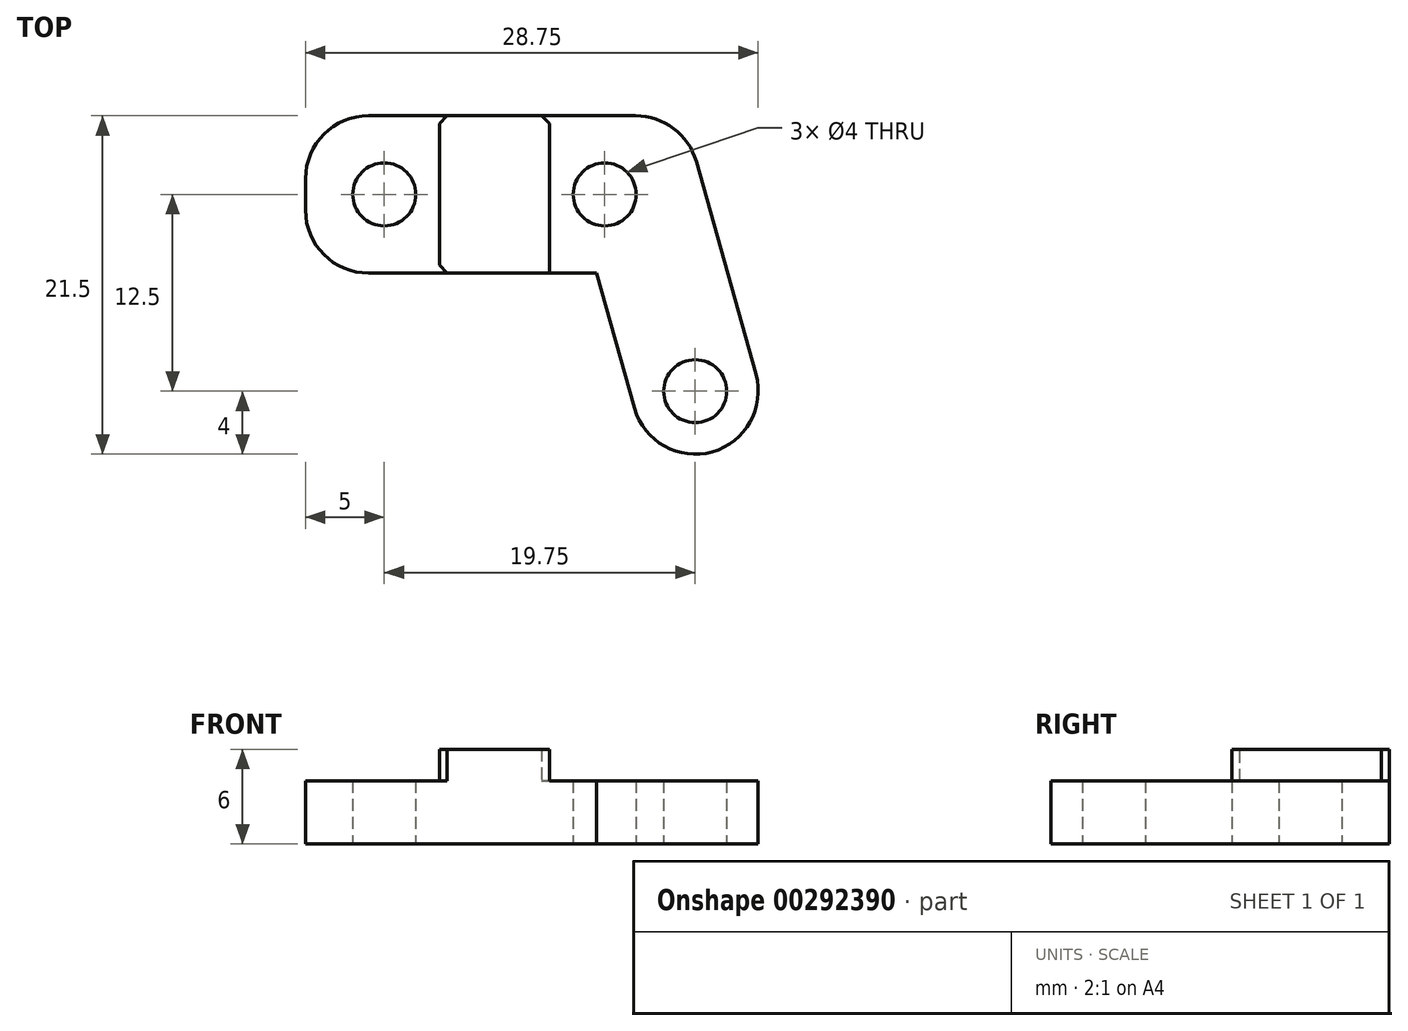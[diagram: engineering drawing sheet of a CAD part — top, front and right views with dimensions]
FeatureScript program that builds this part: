
annotation { "Feature Type Name" : "Feature", "Feature Type Description" : "" }
export const myFeature = defineFeature(function(context is Context, id is Id, definition is map)
    precondition{}
    {
        {
            var Q0;
            Q0=qCreatedBy(makeId("Top.planeOp"),FACE);
            var sketch = newSketch(context, id + "F0", { "sketchPlane" : qUnion([Q0])});
            skLineSegment(sketch, "E0.bottom", {"start": v(0, 0) * mm, "end": v(24, 0) * mm});
            skLineSegment(sketch, "E0.top", {"start": v(0, 10) * mm, "end": v(24, 10) * mm});
            skLineSegment(sketch, "E0.left", {"start": v(0, 0) * mm, "end": v(0, 10) * mm});
            skLineSegment(sketch, "E0.right", {"start": v(24, 0) * mm, "end": v(24, 10) * mm});
            skCircle(sketch, "E1", {"center": v(5, 5) * mm, "radius": 2 * mm});
            skPoint(sketch, "E1.centerSnap0", {"position": v(0, 5) * mm});
            skCircle(sketch, "E2", {"center": v(19, 5) * mm, "radius": 2 * mm});
            skSolve(sketch);
        }
        {
            var Q0;
            Q0 = qSketchRegion(id + "F0", true);
            extrude(context, id + "F1", {"entities" : qUnion([Q0]), "depth" : 4 * mm});
        }
        {
            var Q0;
            Q0=makeQuery(id+"F1.opExtrude","CAP_FACE",FACE,{"disambiguationData":[OSD([sQuery(id+"F0.wireOp",EDGE,"E0.bottom"),sQuery(id+"F0.wireOp",EDGE,"E0.top"),sQuery(id+"F0.wireOp",EDGE,"E0.left"),sQuery(id+"F0.wireOp",EDGE,"E0.right"),sQuery(id+"F0.wireOp",EDGE,"E1"),sQuery(id+"F0.wireOp",EDGE,"E2")])],"isStart":false});
            var sketch = newSketch(context, id + "F2", { "sketchPlane" : qUnion([Q0])});
            skLineSegment(sketch, "E3.bottom", {"start": v(8.5, 10) * mm, "end": v(15.5, 10) * mm});
            skLineSegment(sketch, "E3.top", {"start": v(8.5, 0) * mm, "end": v(15.5, 0) * mm});
            skLineSegment(sketch, "E3.left", {"start": v(8.5, 10) * mm, "end": v(8.5, 0) * mm});
            skLineSegment(sketch, "E3.right", {"start": v(15.5, 10) * mm, "end": v(15.5, 0) * mm});
            skCircle(sketch, "E4.0", {"center": v(5, 5) * mm, "radius": 2 * mm, "construction": true});
            skSolve(sketch);
        }
        {
            var Q0;
            Q0=makeQuery(id+"F2.imprint","IMPRINT",FACE,{"disambiguationData":[TD([[makeQuery(id+"F2.imprint","IMPRINT",EDGE,{"derivedFrom":sQuery(id+"F2.wireOp",EDGE,"E3.bottom")}),-1.0]])]});
            extrude(context, id + "F3", {"entities" : qUnion([Q0]), "operationType" : NewBodyOperationType.ADD, "depth" : 2 * mm});
        }
        {
            var Q0;
            Q0=makeQuery(id+"F1.opExtrude","CAP_FACE",FACE,{"disambiguationData":[OSD([sQuery(id+"F0.wireOp",EDGE,"E0.bottom"),sQuery(id+"F0.wireOp",EDGE,"E0.top"),sQuery(id+"F0.wireOp",EDGE,"E0.left"),sQuery(id+"F0.wireOp",EDGE,"E0.right"),sQuery(id+"F0.wireOp",EDGE,"E1"),sQuery(id+"F0.wireOp",EDGE,"E2")])],"isStart":true});
            var sketch = newSketch(context, id + "F4", { "sketchPlane" : qUnion([Q0])});
            skCircle(sketch, "E5", {"center": v(24.75, 7.5) * mm, "radius": 4 * mm});
            skCircle(sketch, "E6", {"center": v(24.75, 7.5) * mm, "radius": 2 * mm});
            skCircle(sketch, "E7.0", {"center": v(19, -5) * mm, "radius": 2 * mm, "construction": true});
            skLineSegment(sketch, "E8", {"start": v(24, -10) * mm, "end": v(28.9, 7.52) * mm});
            skLineSegment(sketch, "E9", {"start": v(18.5, 0) * mm, "end": v(20.9, 8.58) * mm});
            skLineSegment(sketch, "E10.0", {"start": v(18.5, 0) * mm, "end": v(24, 0) * mm});
            skLineSegment(sketch, "E11.0", {"start": v(24, 0) * mm, "end": v(24, -10) * mm});
            skPoint(sketch, "E12.orphan", {"position": v(0, 0) * mm});
            skSolve(sketch);
        }
        {
            var Q0;
            Q0 = qSketchRegion(id + "F4", true);
            var Q1;
            {var subQ0=sQuery(id+"F0.wireOp",EDGE,"E2");var subQ1=sQuery(id+"F0.wireOp",EDGE,"E0.top");var subQ2=sQuery(id+"F0.wireOp",EDGE,"E0.right");var subQ3=sQuery(id+"F0.wireOp",EDGE,"E0.bottom");Q1=makeQuery(id+"F3.boolean.opBoolean","SPLIT",FACE,{"disambiguationData":[TD([makeQuery(id+"F1.opExtrude","SWEPT_FACE",FACE,{"disambiguationData":[OSD([subQ2])]})])],"derivedFrom":makeQuery(id+"F1.opExtrude","CAP_FACE",FACE,{"disambiguationData":[OSD([subQ3,subQ1,sQuery(id+"F0.wireOp",EDGE,"E0.left"),subQ2,sQuery(id+"F0.wireOp",EDGE,"E1"),subQ0])],"isStart":false})});}
            extrude(context, id + "F5", {"entities" : qUnion([Q0]), "operationType" : NewBodyOperationType.ADD, "endBound" : BoundingType.UP_TO_SURFACE, "oppositeDirection" : true, "endBoundEntityFace" : qUnion([Q1]), "depth" : 25 * mm});
        }
        {
            var Q0;
            {var subQ0=sQuery(id+"F0.wireOp",EDGE,"E0.top");Q0=makeQuery(id+"F5.boolean.opBoolean","MERGE",EDGE,{"derivedFrom":[makeQuery(id+"F1.opExtrude","SWEPT_EDGE",EDGE,{"disambiguationData":[OSD([subQ0,sQuery(id+"F0.wireOp",EDGE,"E0.right")])]}),makeQuery(id+"F5.opExtrude","SWEPT_EDGE",EDGE,{"disambiguationData":[OSD([subQ0,sQuery(id+"F4.wireOp",EDGE,"E8"),sQuery(id+"F4.wireOp",EDGE,"E11.0")])]})]});}
            var Q1;
            Q1=makeQuery(id+"F5.opExtrude","SWEPT_EDGE",EDGE,{"disambiguationData":[OSD([sQuery(id+"F0.wireOp",EDGE,"E0.bottom"),sQuery(id+"F4.wireOp",EDGE,"E9"),sQuery(id+"F4.wireOp",EDGE,"E10.0")])]});
            var Q2;
            Q2=makeQuery(id+"F1.opExtrude","SWEPT_EDGE",EDGE,{"disambiguationData":[OSD([sQuery(id+"F0.wireOp",EDGE,"E0.bottom"),sQuery(id+"F0.wireOp",EDGE,"E0.left")])]});
            var Q3;
            Q3=makeQuery(id+"F1.opExtrude","SWEPT_EDGE",EDGE,{"disambiguationData":[OSD([sQuery(id+"F0.wireOp",EDGE,"E0.top"),sQuery(id+"F0.wireOp",EDGE,"E0.left")])]});
            fillet(context, id + "F6", {"entities" : qUnion([Q0, Q1, Q2, Q3]), "radius" : 4 * mm, "tangentPropagation" : true, "allowEdgeOverflow" : false});
        }
        {
            var Q0;
            Q0=makeQuery(id+"F3.opExtrude","SWEPT_EDGE",EDGE,{"disambiguationData":[OSD([sQuery(id+"F0.wireOp",EDGE,"E0.bottom"),sQuery(id+"F2.wireOp",EDGE,"E3.top"),sQuery(id+"F2.wireOp",EDGE,"E3.left")])]});
            var Q1;
            Q1=makeQuery(id+"F6.opFillet","BLEND_EDGE",EDGE,{"blendedFrom":[makeQuery(id+"F5.opExtrude","SWEPT_EDGE",EDGE,{"disambiguationData":[OSD([sQuery(id+"F0.wireOp",EDGE,"E0.bottom"),sQuery(id+"F4.wireOp",EDGE,"E9"),sQuery(id+"F4.wireOp",EDGE,"E10.0")])]}),makeQuery(id+"F3.opExtrude","SWEPT_FACE",FACE,{"disambiguationData":[OSD([sQuery(id+"F2.wireOp",EDGE,"E3.right")])]})],"blendedInto":[makeQuery(id+"F3.opExtrude","SWEPT_FACE",FACE,{"disambiguationData":[OSD([sQuery(id+"F2.wireOp",EDGE,"E3.right")])]})]});
            var Q2;
            Q2=makeQuery(id+"F3.opExtrude","SWEPT_EDGE",EDGE,{"disambiguationData":[OSD([sQuery(id+"F0.wireOp",EDGE,"E0.top"),sQuery(id+"F2.wireOp",EDGE,"E3.bottom"),sQuery(id+"F2.wireOp",EDGE,"E3.right")])]});
            var Q3;
            Q3=makeQuery(id+"F3.opExtrude","SWEPT_EDGE",EDGE,{"disambiguationData":[OSD([sQuery(id+"F0.wireOp",EDGE,"E0.top"),sQuery(id+"F2.wireOp",EDGE,"E3.bottom"),sQuery(id+"F2.wireOp",EDGE,"E3.left")])]});
            chamfer(context, id + "F7", {"entities" : qUnion([Q0, Q1, Q2, Q3]), "width" : .5 * mm, "tangentPropagation" : true});
        }
    });
